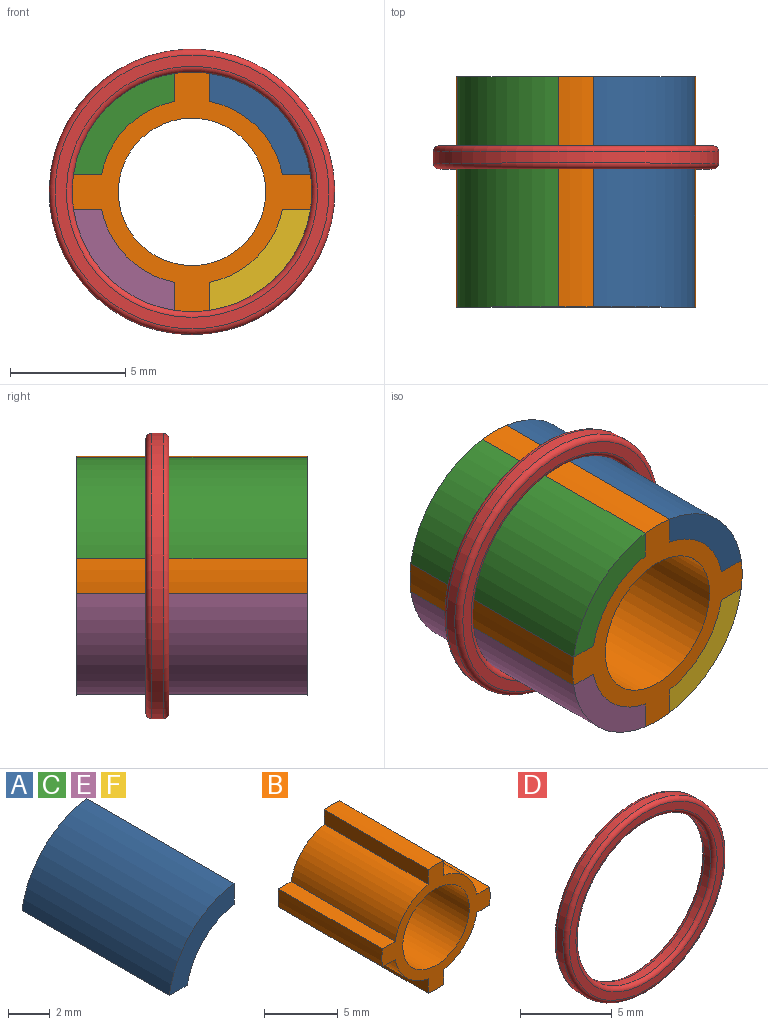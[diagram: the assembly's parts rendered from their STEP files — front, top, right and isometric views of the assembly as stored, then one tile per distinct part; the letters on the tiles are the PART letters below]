
ASSEMBLY  parts=6 mates=5
PART A: 6 faces, bbox 4.4x10x4.4 mm
  f0: cylinder r=5.2mm len=10mm, axis (0,1,0), area 66.6mm2, adj f1,f3,f4,f5
  f1: plane 10x1.22mm, normal (0,0,-1), area 12.2mm2, adj f0,f2,f4,f5
  f2: cylinder r=4mm len=10mm, axis (0,1,0), area 47.7mm2, adj f1,f3,f4,f5
  f3: plane 10x1.22mm, normal (1,0,0), area 12.2mm2, adj f0,f2,f4,f5
  f4: plane 4.4x4.4mm, normal (0,-1,0), area 6.9mm2, adj f0,f1,f2,f3
  f5: plane 4.4x4.4mm, normal (0,1,0), area 6.9mm2, adj f0,f1,f2,f3
PART B: 19 faces, bbox 10.4x10x10.4 mm
  f0: cylinder r=4mm len=10mm, axis (0,1,0), area 47.7mm2, adj f1,f16,f17,f18
  f1: plane 10x1.22mm, normal (1,0,0), area 12.2mm2, adj f0,f2,f17,f18
  f2: cylinder r=5.2mm len=10mm, axis (0,1,0), area 15.1mm2, adj f1,f3,f17,f18
  f3: plane 10x1.22mm, normal (-1,0,0), area 12.2mm2, adj f2,f4,f17,f18
  f4: cylinder r=4mm len=10mm, axis (0,1,0), area 47.7mm2, adj f3,f5,f17,f18
  f5: plane 10x1.22mm, normal (0,0,1), area 12.2mm2, adj f4,f6,f17,f18
  f6: cylinder r=5.2mm len=10mm, axis (0,1,0), area 15.1mm2, adj f5,f7,f17,f18
  f7: plane 10x1.22mm, normal (0,0,-1), area 12.2mm2, adj f6,f8,f17,f18
  f8: cylinder r=4mm len=10mm, axis (0,1,0), area 47.7mm2, adj f7,f9,f17,f18
  f9: plane 10x1.22mm, normal (-1,0,0), area 12.2mm2, adj f8,f10,f17,f18
  f10: cylinder r=5.2mm len=10mm, axis (0,1,0), area 15.1mm2, adj f9,f11,f17,f18
  f11: plane 10x1.22mm, normal (1,0,0), area 12.2mm2, adj f10,f12,f17,f18
  f12: cylinder r=4mm len=10mm, axis (0,1,0), area 47.7mm2, adj f11,f13,f17,f18
  f13: plane 10x1.22mm, normal (0,0,-1), area 12.2mm2, adj f12,f14,f17,f18
  f14: cylinder r=5.2mm len=10mm, axis (0,1,0), area 15.1mm2, adj f13,f16,f17,f18
  f15: cylinder r=3.2mm len=10mm, axis (0,1,0), area 201.1mm2, adj f17,f18
  f16: plane 10x1.22mm, normal (0,0,1), area 12.2mm2, adj f0,f14,f17,f18
  f17: plane 10.4x10.4mm, normal (0,-1,0), area 25.3mm2, adj f0,f1,f2,f3,f4,f5,f6,f7
  f18: plane 10.4x10.4mm, normal (0,1,0), area 25.3mm2, adj f0,f1,f2,f3,f4,f5,f6,f7
PART C: same geometry as A
PART D: 8 faces, bbox 13.4x1x13.4 mm
  f0: cylinder r=5.2mm len=10.4mm, axis (0,1,0), area 16.3mm2, adj f4,f6
  f1: cylinder r=6.2mm len=12.4mm, axis (0,1,0), area 19.5mm2, adj f5,f7
  f2: plane 11.9x11.9mm, normal (0,-1,0), area 17.9mm2, adj f6,f7
  f3: plane 11.9x11.9mm, normal (0,1,0), area 17.9mm2, adj f4,f5
  f4: torus R=5.45mm, axis (0,-1,0), area 13.1mm2, adj f0,f3
  f5: torus R=5.95mm, axis (0,-1,0), area 15.1mm2, adj f1,f3
  f6: torus R=5.45mm, axis (0,-1,0), area 13.1mm2, adj f0,f2
  f7: torus R=5.95mm, axis (0,-1,0), area 15.1mm2, adj f1,f2
PART E: same geometry as A
PART F: same geometry as A
PLACE A rot(axis=(0,1,0),90deg) t=(0,0,0)mm
PLACE B at identity fixed
PLACE C at identity
PLACE D t=(0,-3,0)mm
PLACE E rot(axis=(0,-1,0),90deg) t=(0,0,0)mm
PLACE F rot(axis=(0,-1,0),180deg) t=(0,0,0)mm
MATE planar B.f0 <-> A.f0  axis (0,1,0) through (0,0,0)mm
MATE cylindrical B.f0 <-> D.f0  axis (0,1,0) through (0,-5,0)mm
MATE planar B.f1 <-> A.f1  axis (1,0,0) through (0.75,-5,4.54)mm
MATE cylindrical B.f0 <-> F.f0  axis (0,1,0) through (0,-5,0)mm
MATE parallel B.f0 <-> D.f0  axis (0,1,0) through (0,0,0)mm
